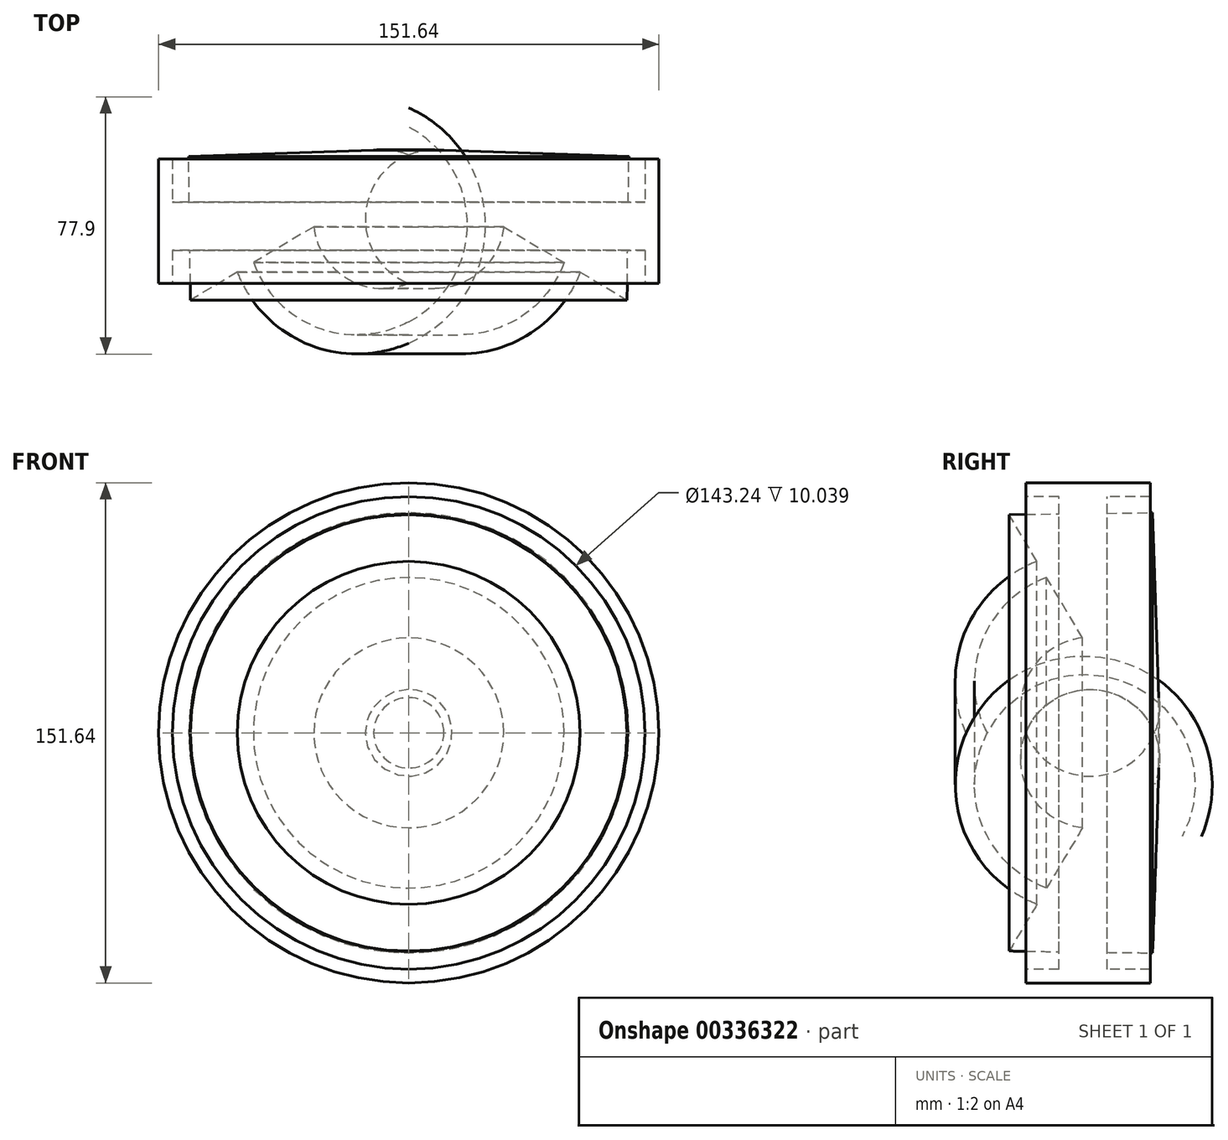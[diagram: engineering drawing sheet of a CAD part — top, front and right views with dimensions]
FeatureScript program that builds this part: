
annotation { "Feature Type Name" : "Feature", "Feature Type Description" : "" }
export const myFeature = defineFeature(function(context is Context, id is Id, definition is map)
    precondition{}
    {
        {
            var Q0;
            Q0=qCreatedBy(makeId("Top.planeOp"),FACE);
            var sketch = newSketch(context, id + "F0", { "sketchPlane" : qUnion([Q0])});
            skLineSegment(sketch, "E0", {"start": v(0, 0) * mm, "end": v(0, 39.04) * mm});
            skLineSegment(sketch, "E1.bottom", {"start": v(-75.82, 37.75) * mm, "end": v(-71.62, 37.75) * mm});
            skLineSegment(sketch, "E1.top", {"start": v(-75.82, 0) * mm, "end": v(-71.62, 0) * mm});
            skLineSegment(sketch, "E1.left", {"start": v(-75.82, 37.75) * mm, "end": v(-75.82, 0) * mm});
            skLineSegment(sketch, "E1.right", {"start": v(-71.62, 37.75) * mm, "end": v(-71.62, 24.64) * mm});
            skLineSegment(sketch, "E2.1", {"start": v(-28.78, 17.21) * mm, "end": v(-47.07, 6.33) * mm});
            skLineSegment(sketch, "E2.2", {"start": v(-66.14, -5.02) * mm, "end": v(-66.34, 10.04) * mm});
            skPoint(sketch, "E2.0.midPoint", {"position": v(-47.75, 27.83) * mm});
            skLineSegment(sketch, "E3.bottom", {"start": v(-71.62, 24.64) * mm, "end": v(-66.34, 24.64) * mm});
            skLineSegment(sketch, "E3.top", {"start": v(-71.62, 10.04) * mm, "end": v(-66.34, 10.04) * mm});
            skLineSegment(sketch, "E4.trimOffspring", {"start": v(-71.62, 10.04) * mm, "end": v(-71.62, 0) * mm});
            skLineSegment(sketch, "E5.trimOffspring", {"start": v(-66.53, 24.64) * mm, "end": v(-66.71, 38.45) * mm});
            skArc(sketch, "E6", {"start": v(0, 39.04) * mm, "mid": v(-28.9, 19.52) * mm, "end": v(0, 0) * mm});
            skLineSegment(sketch, "E7", {"start": v(0, -18.07) * mm, "end": v(0, -11.61) * mm});
            skLineSegment(sketch, "E8.trimOffspring", {"start": v(-51.97, 3.41) * mm, "end": v(-66.14, -5.02) * mm});
            skLineSegment(sketch, "E9.trimOffspring", {"start": v(-47.75, 27.83) * mm, "end": v(-47.65, 27.78) * mm});
            skArc(sketch, "E10.trimOffspring", {"start": v(-51.97, 3.41) * mm, "mid": v(-30.57, -18.41) * mm, "end": v(0, -18.07) * mm});
            skArc(sketch, "E11.trimOffspring", {"start": v(-47.07, 6.33) * mm, "mid": v(-27.61, -13.34) * mm, "end": v(0, -11.61) * mm});
            skLineSegment(sketch, "E12", {"start": v(-47.65, 27.78) * mm, "end": v(-47.75, 27.83) * mm});
            skPoint(sketch, "E13.end.orphan", {"position": v(0, 53.23) * mm});
            skPoint(sketch, "E14.start.orphan", {"position": v(0, 47.43) * mm});
            skLineSegment(sketch, "E15", {"start": v(-10.65, 40.38) * mm, "end": v(-66.71, 38.45) * mm});
            skSolve(sketch);
        }
        {
            var Q0;
            Q0 = qSketchRegion(id + "F0", true);
            var Q1;
            Q1=sQuery(id+"F0.wireOp",EDGE,"E0");
            revolve(context, id + "F1", {"entities" : qUnion([Q0]), "axis" : qUnion([Q1]), "revolveType" : RevolveType.FULL});
        }
    });
